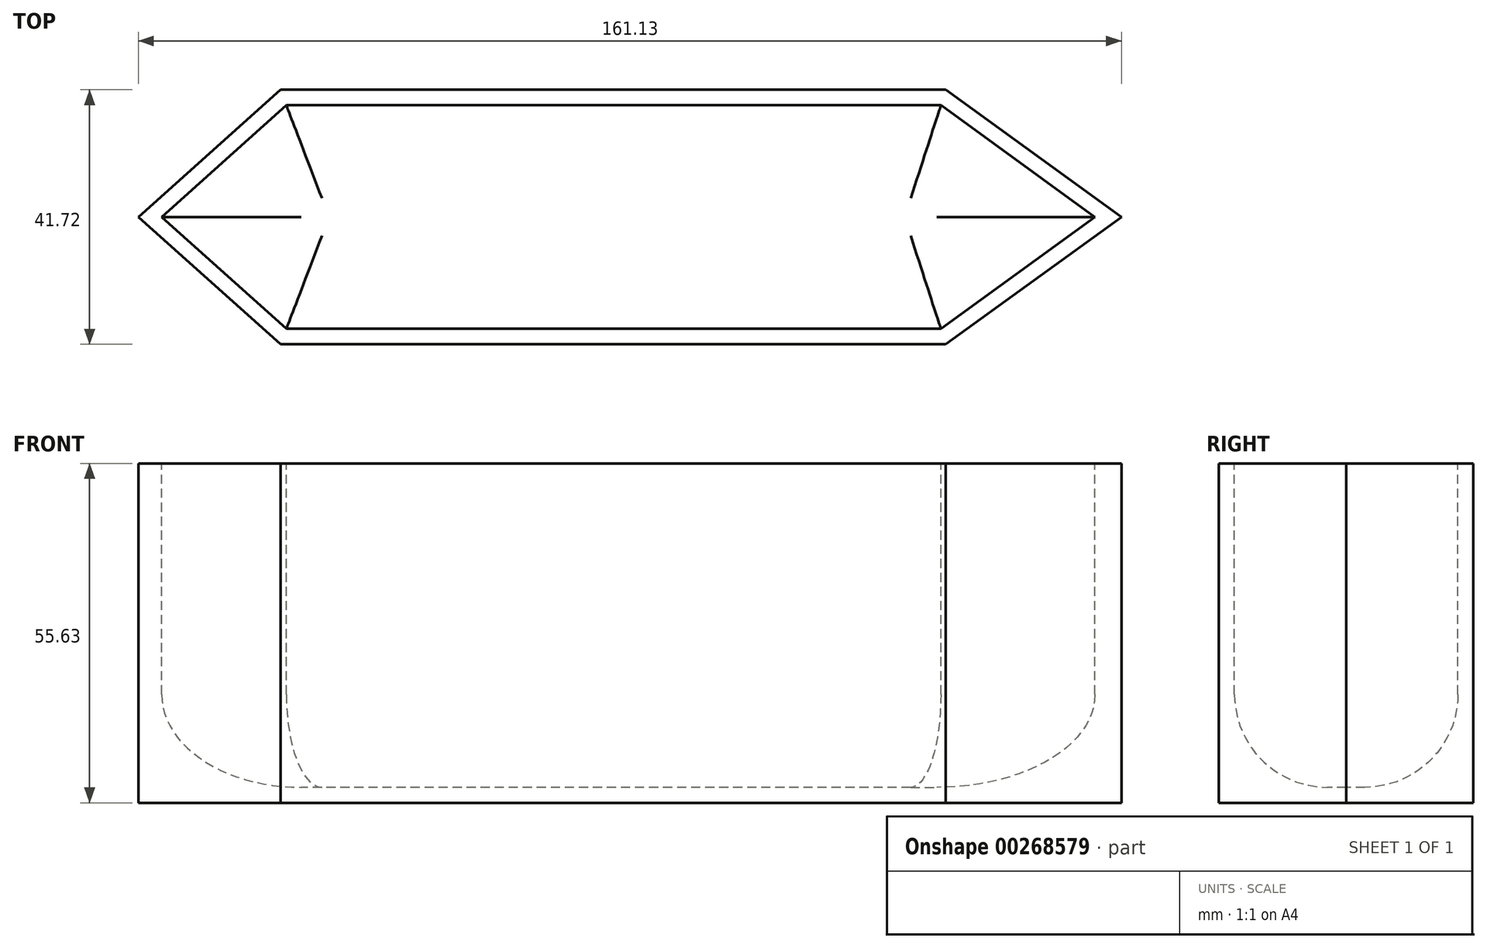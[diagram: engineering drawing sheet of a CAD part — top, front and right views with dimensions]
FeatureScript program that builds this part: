
annotation { "Feature Type Name" : "Feature", "Feature Type Description" : "" }
export const myFeature = defineFeature(function(context is Context, id is Id, definition is map)
    precondition{}
    {
        {
            var Q0;
            Q0=qCreatedBy(makeId("Top.planeOp"),FACE);
            var sketch = newSketch(context, id + "F0", { "sketchPlane" : qUnion([Q0])});
            skLineSegment(sketch, "E0.bottom", {"start": v(54.54, -20.86) * mm, "end": v(-54.54, -20.86) * mm});
            skLineSegment(sketch, "E0.top", {"start": v(54.54, 20.86) * mm, "end": v(-54.54, 20.86) * mm});
            skPoint(sketch, "E0.middle", {"position": v(0, 0) * mm});
            skLineSegment(sketch, "E1", {"start": v(-54.54, 20.86) * mm, "end": v(-77.82, 0) * mm});
            skLineSegment(sketch, "E2", {"start": v(-77.82, 0) * mm, "end": v(-54.54, -20.86) * mm});
            skLineSegment(sketch, "E3", {"start": v(54.54, 20.86) * mm, "end": v(83.31, 0) * mm});
            skLineSegment(sketch, "E4", {"start": v(83.31, 0) * mm, "end": v(54.54, -20.86) * mm});
            skSolve(sketch);
        }
        {
            var Q0;
            Q0=makeQuery(id+"F0.imprint","IMPRINT",FACE,{"disambiguationData":[TD([[makeQuery(id+"F0.imprint","IMPRINT",EDGE,{"derivedFrom":sQuery(id+"F0.wireOp",EDGE,"E0.bottom")}),-1.0]])]});
            extrude(context, id + "F1", {"entities" : qUnion([Q0]), "oppositeDirection" : true, "depth" : 55.63 * mm});
        }
        {
            var Q0;
            Q0=makeQuery(id+"F1.opExtrude","CAP_FACE",FACE,{"disambiguationData":[OSD([sQuery(id+"F0.wireOp",EDGE,"E0.bottom"),sQuery(id+"F0.wireOp",EDGE,"E0.top"),sQuery(id+"F0.wireOp",EDGE,"E1"),sQuery(id+"F0.wireOp",EDGE,"E2"),sQuery(id+"F0.wireOp",EDGE,"E3"),sQuery(id+"F0.wireOp",EDGE,"E4")])],"isStart":true});
            shell(context, id + "F2", {"entities" : qUnion([Q0]), "thickness" : 2.54 * mm});
        }
        {
            var Q0;
            Q0=makeQuery(id+"F2.opShell","OFFSET_FACE",FACE,{"disambiguationData":[OSD([sQuery(id+"F0.wireOp",EDGE,"E0.bottom"),sQuery(id+"F0.wireOp",EDGE,"E0.top"),sQuery(id+"F0.wireOp",EDGE,"E1"),sQuery(id+"F0.wireOp",EDGE,"E2"),sQuery(id+"F0.wireOp",EDGE,"E3"),sQuery(id+"F0.wireOp",EDGE,"E4")])]});
            fillet(context, id + "F3", {"entities" : qUnion([Q0]), "radius" : 15.24 * mm, "tangentPropagation" : true, "allowEdgeOverflow" : false});
        }
    });
